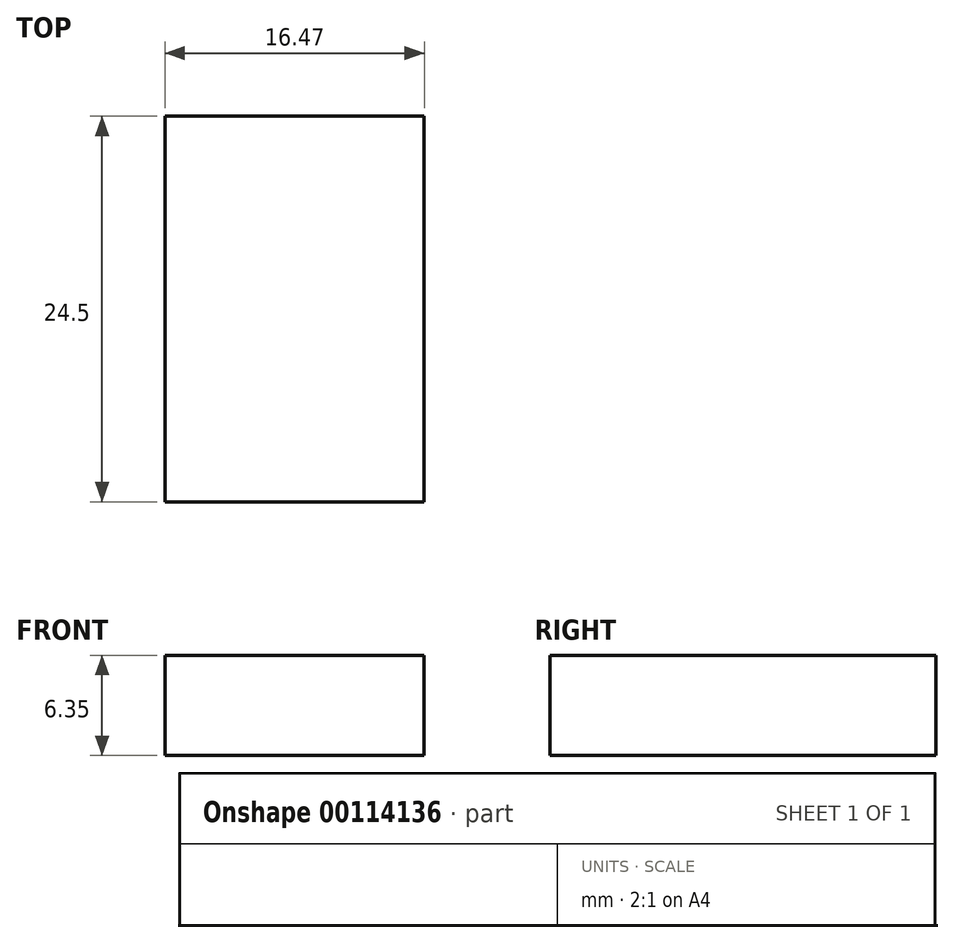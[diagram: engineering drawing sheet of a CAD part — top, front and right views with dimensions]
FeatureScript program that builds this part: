
annotation { "Feature Type Name" : "Feature", "Feature Type Description" : "" }
export const myFeature = defineFeature(function(context is Context, id is Id, definition is map)
    precondition{}
    {
        {
            var Q0;
            Q0=qCreatedBy(makeId("Top.planeOp"),FACE);
            var sketch = newSketch(context, id + "F0", { "sketchPlane" : qUnion([Q0])});
            skLineSegment(sketch, "E0.bottom", {"start": v(-7.99, 12.48) * mm, "end": v(8.48, 12.48) * mm});
            skLineSegment(sketch, "E0.top", {"start": v(-7.99, -12.02) * mm, "end": v(8.48, -12.02) * mm});
            skLineSegment(sketch, "E0.left", {"start": v(-7.99, 12.48) * mm, "end": v(-7.99, -12.02) * mm});
            skLineSegment(sketch, "E0.right", {"start": v(8.48, 12.48) * mm, "end": v(8.48, -12.02) * mm});
            skSolve(sketch);
        }
        {
            var Q0;
            Q0=makeQuery(id+"F0.imprint","IMPRINT",FACE,{"disambiguationData":[TD([[makeQuery(id+"F0.imprint","IMPRINT",EDGE,{"derivedFrom":sQuery(id+"F0.wireOp",EDGE,"E0.bottom")}),-1.0]])]});
            extrude(context, id + "F1", {"entities" : qUnion([Q0]), "depth" : 6.35 * mm});
        }
    });
